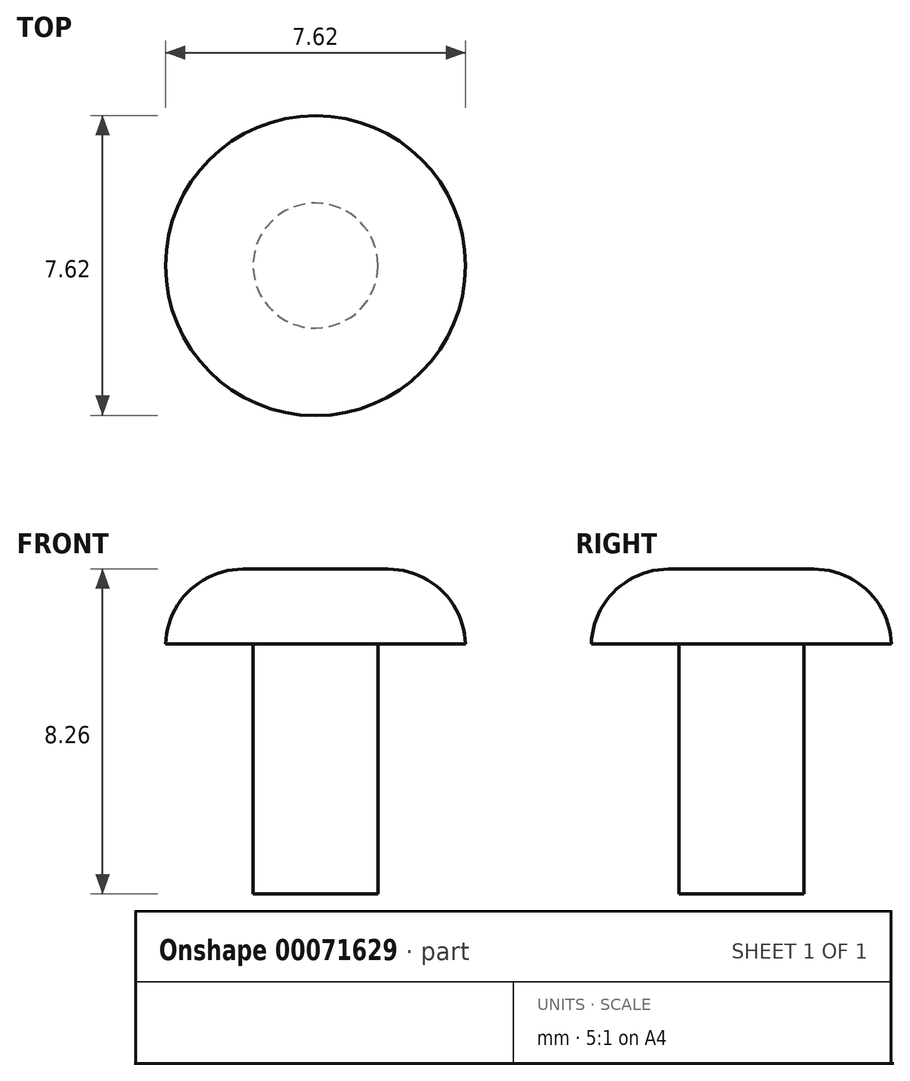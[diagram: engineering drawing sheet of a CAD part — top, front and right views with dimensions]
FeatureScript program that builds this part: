
annotation { "Feature Type Name" : "Feature", "Feature Type Description" : "" }
export const myFeature = defineFeature(function(context is Context, id is Id, definition is map)
    precondition{}
    {
        {
            var Q0;
            Q0=qCreatedBy(makeId("Top.planeOp"),FACE);
            var sketch = newSketch(context, id + "F0", { "sketchPlane" : qUnion([Q0])});
            skCircle(sketch, "E0", {"center": v(-68.4, -61.13) * mm, "radius": 1.59 * mm});
            skSolve(sketch);
        }
        {
            var Q0;
            Q0 = qSketchRegion(id + "F0", true);
            extrude(context, id + "F1", {"entities" : qUnion([Q0]), "depth" : 6.35 * mm});
        }
        {
            var Q0;
            Q0=makeQuery(id+"F1.opExtrude","CAP_FACE",FACE,{"disambiguationData":[OSD([sQuery(id+"F0.wireOp",EDGE,"E0")])],"isStart":false});
            var sketch = newSketch(context, id + "F2", { "sketchPlane" : qUnion([Q0])});
            skCircle(sketch, "E1", {"center": v(-68.4, -61.13) * mm, "radius": 5.36 * mm});
            skSolve(sketch);
        }
        {
            var Q0;
            Q0=makeQuery(id+"F2.imprint","IMPRINT",FACE,{"disambiguationData":[TD([[makeQuery(id+"F2.imprint","IMPRINT",EDGE,{"derivedFrom":sQuery(id+"F2.wireOp",EDGE,"E1")}),1.0]])]});
            extrude(context, id + "F3", {"entities" : qUnion([Q0]), "depth" : 0.79 * mm});
        }
        {
            var Q0;
            Q0=makeQuery(id+"F3.opExtrude","SWEPT_BODY",BODY,{"disambiguationData":[OSD([sQuery(id+"F0.wireOp",EDGE,"E0"),sQuery(id+"F2.wireOp",EDGE,"E1")])]});
            var Q1;
            Q1=makeQuery(id+"F1.opExtrude","SWEPT_BODY",BODY,{"disambiguationData":[OSD([sQuery(id+"F0.wireOp",EDGE,"E0")])]});
            deleteBodies(context, id + "F4", {"entities" : qUnion([Q0, Q1])});
        }
        {
            var Q0;
            Q0=qCreatedBy(makeId("Top.planeOp"),FACE);
            var sketch = newSketch(context, id + "F5", { "sketchPlane" : qUnion([Q0])});
            skCircle(sketch, "E2", {"center": v(-68.15, -56.63) * mm, "radius": 1.59 * mm});
            skSolve(sketch);
        }
        {
            var Q0;
            Q0 = qSketchRegion(id + "F5", true);
            extrude(context, id + "F6", {"entities" : qUnion([Q0]), "depth" : 6.35 * mm});
        }
        {
            var Q0;
            Q0=makeQuery(id+"F6.opExtrude","CAP_FACE",FACE,{"disambiguationData":[OSD([sQuery(id+"F5.wireOp",EDGE,"E2")])],"isStart":false});
            var sketch = newSketch(context, id + "F7", { "sketchPlane" : qUnion([Q0])});
            skCircle(sketch, "E3", {"center": v(-68.15, -56.63) * mm, "radius": 3.81 * mm});
            skSolve(sketch);
        }
        {
            var Q0;
            Q0 = qSketchRegion(id + "F7", true);
            extrude(context, id + "F8", {"entities" : qUnion([Q0]), "operationType" : NewBodyOperationType.ADD, "depth" : 1.9 * mm});
        }
        {
            var Q0;
            Q0=makeQuery(id+"F8.opExtrude","CAP_EDGE",EDGE,{"disambiguationData":[OSD([sQuery(id+"F7.wireOp",EDGE,"E3")])],"isStart":false});
            fillet(context, id + "F9", {"entities" : qUnion([Q0]), "radius" : 1.96 * mm, "tangentPropagation" : true, "allowEdgeOverflow" : false});
        }
    });
